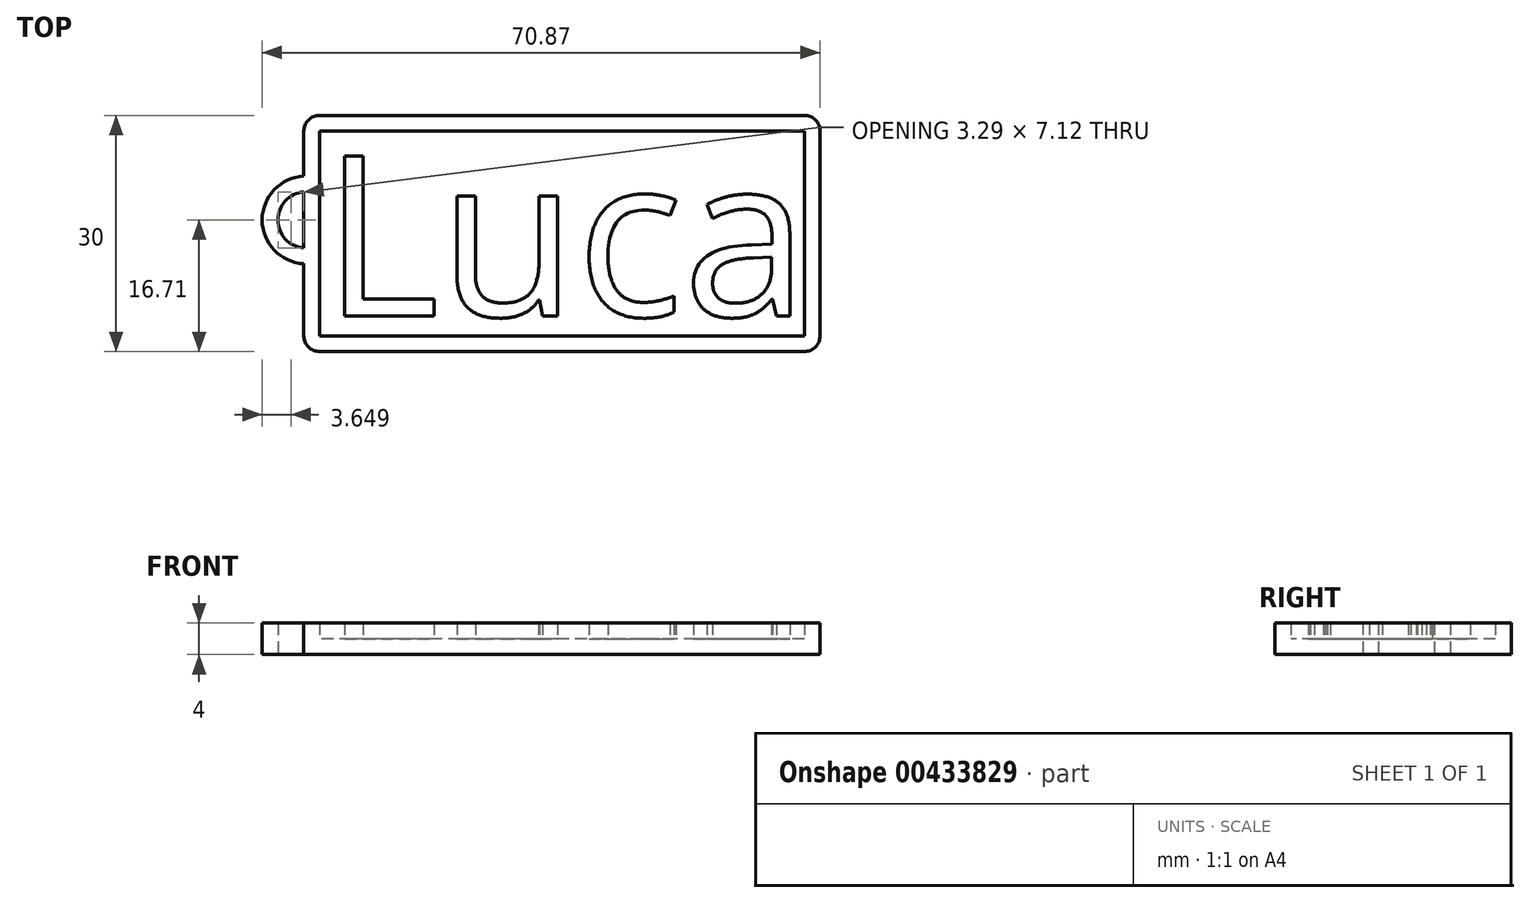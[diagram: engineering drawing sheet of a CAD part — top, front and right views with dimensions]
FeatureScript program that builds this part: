
annotation { "Feature Type Name" : "Feature", "Feature Type Description" : "" }
export const myFeature = defineFeature(function(context is Context, id is Id, definition is map)
    precondition{}
    {
        {
            var Q0;
            Q0=qCreatedBy(makeId("Top.planeOp"),FACE);
            var sketch = newSketch(context, id + "F0", { "sketchPlane" : qUnion([Q0])});
            skLineSegment(sketch, "E0.bottom", {"start": v(30.79, 13.29) * mm, "end": v(-30.79, 13.29) * mm});
            skLineSegment(sketch, "E0.top", {"start": v(30.79, -16.71) * mm, "end": v(-30.79, -16.71) * mm});
            skLineSegment(sketch, "E0.left", {"start": v(32.79, 11.29) * mm, "end": v(32.79, -14.71) * mm});
            skLineSegment(sketch, "E0.right", {"start": v(-32.79, 11.29) * mm, "end": v(-32.79, -14.71) * mm});
            skPoint(sketch, "E0.middle", {"position": v(0, -1.71) * mm});
            skPoint(sketch, "E1.visualSharp", {"position": v(-32.79, 13.29) * mm});
            skArc(sketch, "E1.filletArc", {"start": v(-30.79, 13.29) * mm, "mid": v(-32.2, 12.7) * mm, "end": v(-32.79, 11.29) * mm});
            skPoint(sketch, "E2.visualSharp", {"position": v(32.79, 13.29) * mm});
            skArc(sketch, "E2.filletArc", {"start": v(32.79, 11.29) * mm, "mid": v(32.2, 12.7) * mm, "end": v(30.79, 13.29) * mm});
            skPoint(sketch, "E3.visualSharp", {"position": v(32.79, -16.71) * mm});
            skArc(sketch, "E3.filletArc", {"start": v(30.79, -16.71) * mm, "mid": v(32.2, -16.13) * mm, "end": v(32.79, -14.71) * mm});
            skPoint(sketch, "E4.visualSharp", {"position": v(-32.79, -16.71) * mm});
            skArc(sketch, "E4.filletArc", {"start": v(-32.79, -14.71) * mm, "mid": v(-32.2, -16.13) * mm, "end": v(-30.79, -16.71) * mm});
            skLineSegment(sketch, "E5.0", {"start": v(30.79, 11.29) * mm, "end": v(-30.79, 11.29) * mm});
            skLineSegment(sketch, "E5.1", {"start": v(30.79, 11.29) * mm, "end": v(30.79, -14.71) * mm});
            skLineSegment(sketch, "E5.2", {"start": v(30.79, -14.71) * mm, "end": v(-30.79, -14.71) * mm});
            skLineSegment(sketch, "E5.3", {"start": v(-30.79, 11.29) * mm, "end": v(-30.79, -14.71) * mm});
            skSolve(sketch);
        }
        {
            var Q0;
            Q0=makeQuery(id+"F0.imprint","IMPRINT",FACE,{"disambiguationData":[TD([[makeQuery(id+"F0.imprint","IMPRINT",EDGE,{"derivedFrom":sQuery(id+"F0.wireOp",EDGE,"E5.0")}),1.0]])]});
            extrude(context, id + "F1", {"entities" : qUnion([Q0]), "depth" : 2 * mm});
        }
        {
            var Q0;
            Q0 = qSketchRegion(id + "F0", true);
            extrude(context, id + "F2", {"entities" : qUnion([Q0]), "operationType" : NewBodyOperationType.ADD, "depth" : 4 * mm});
        }
        {
            var Q0;
            Q0=makeQuery(id+"F1.opExtrude","CAP_FACE",FACE,{"disambiguationData":[OSD([sQuery(id+"F0.wireOp",EDGE,"E5.0"),sQuery(id+"F0.wireOp",EDGE,"E5.1"),sQuery(id+"F0.wireOp",EDGE,"E5.2"),sQuery(id+"F0.wireOp",EDGE,"E5.3")])],"isStart":false});
            var sketch = newSketch(context, id + "F3", { "sketchPlane" : qUnion([Q0])});
            skText(sketch, "E6", { "text": "Luca\n", "fontName": "OpenSans-Regular.ttf"});
            const initialGuessF3  = {"E6": [-0.03039, -0.01221, 1, 0, 0.0205]};
            skSetInitialGuess(sketch, initialGuessF3);
            skSolve(sketch);
        }
        {
            var Q0;
            Q0 = qSketchRegion(id + "F3", true);
            extrude(context, id + "F4", {"entities" : qUnion([Q0]), "operationType" : NewBodyOperationType.ADD, "depth" : 2 * mm});
        }
        {
            var Q0;
            Q0=qCreatedBy(makeId("Top.planeOp"),FACE);
            var sketch = newSketch(context, id + "F5", { "sketchPlane" : qUnion([Q0])});
            skArc(sketch, "E7", {"start": v(-38.08, 0) * mm, "mid": v(-36.44, 3.94) * mm, "end": v(-32.5, 5.57) * mm});
            skArc(sketch, "E8", {"start": v(-38.08, 0) * mm, "mid": v(-36.44, -3.94) * mm, "end": v(-32.5, -5.57) * mm});
            skArc(sketch, "E9.0", {"start": v(-36.08, 0) * mm, "mid": v(-35.03, 2.53) * mm, "end": v(-32.5, 3.57) * mm});
            skArc(sketch, "E9.1", {"start": v(-36.08, 0) * mm, "mid": v(-35.03, -2.53) * mm, "end": v(-32.5, -3.57) * mm});
            skLineSegment(sketch, "E10", {"start": v(-32.5, 5.57) * mm, "end": v(-32.5, 3.57) * mm});
            skLineSegment(sketch, "E11", {"start": v(-32.5, -3.57) * mm, "end": v(-32.5, -5.57) * mm});
            skSolve(sketch);
        }
        {
            var Q0;
            Q0 = qSketchRegion(id + "F5", true);
            extrude(context, id + "F6", {"entities" : qUnion([Q0]), "operationType" : NewBodyOperationType.ADD, "depth" : 4 * mm});
        }
    });
